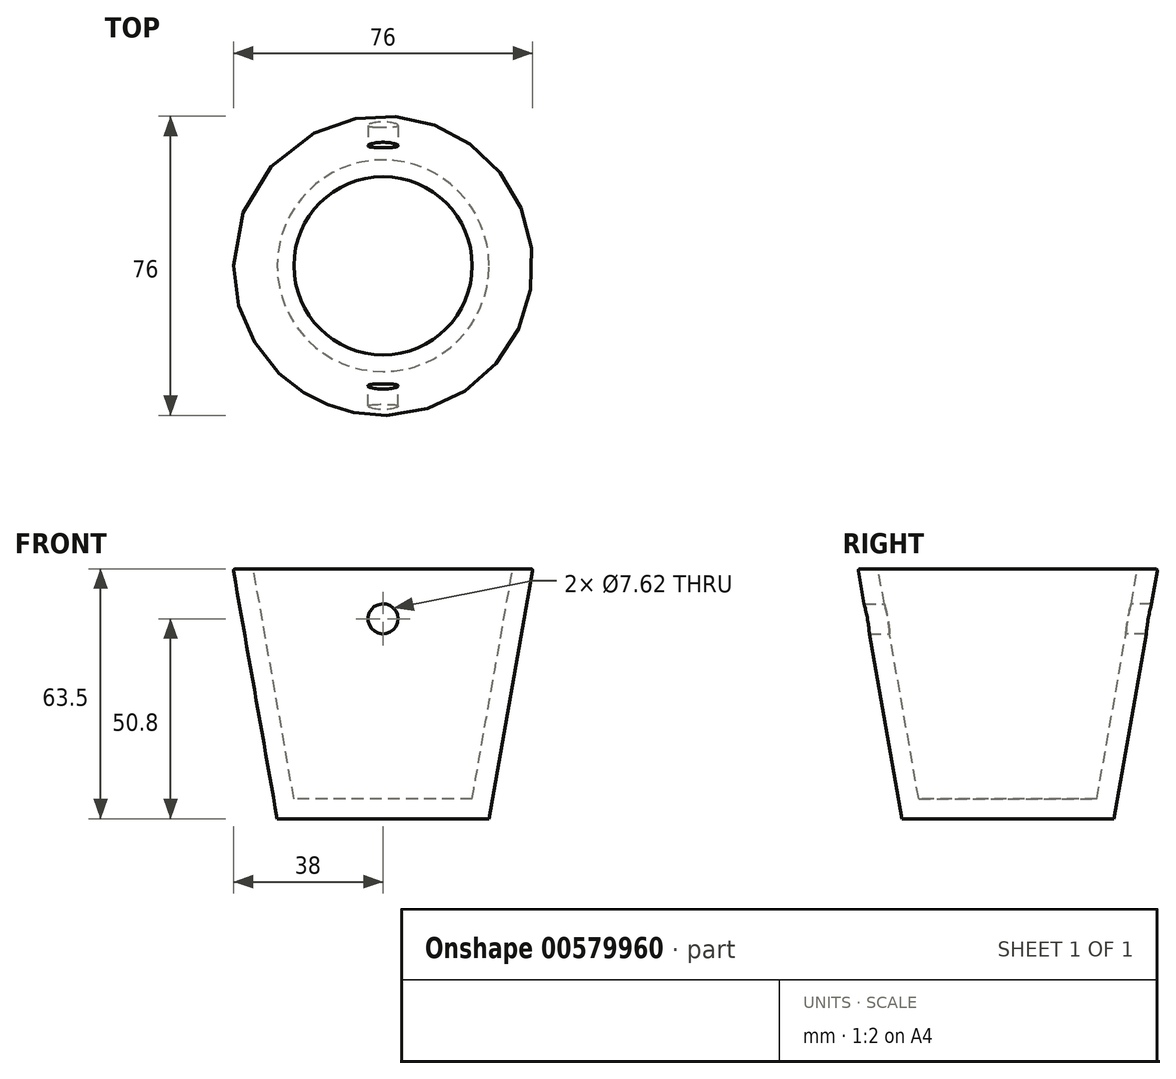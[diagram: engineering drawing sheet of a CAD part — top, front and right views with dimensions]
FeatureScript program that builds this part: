
annotation { "Feature Type Name" : "Feature", "Feature Type Description" : "" }
export const myFeature = defineFeature(function(context is Context, id is Id, definition is map)
    precondition{}
    {
        {
            var Q0;
            Q0=qCreatedBy(makeId("Front.planeOp"),FACE);
            var sketch = newSketch(context, id + "F0", { "sketchPlane" : qUnion([Q0])});
            skLineSegment(sketch, "E0", {"start": v(0, 63.5) * mm, "end": v(-38.1, 63.5) * mm});
            skLineSegment(sketch, "E1", {"start": v(-38.1, 63.5) * mm, "end": v(-26.9, 0) * mm});
            skLineSegment(sketch, "E2", {"start": v(-26.9, 0) * mm, "end": v(0, 0) * mm});
            skLineSegment(sketch, "E3", {"start": v(0, 0) * mm, "end": v(0, 63.5) * mm});
            skSolve(sketch);
        }
        {
            var Q0;
            Q0=makeQuery(id+"F0.imprint","IMPRINT",FACE,{"disambiguationData":[TD([[makeQuery(id+"F0.imprint","IMPRINT",EDGE,{"derivedFrom":sQuery(id+"F0.wireOp",EDGE,"E0")}),1.0]])]});
            var Q1;
            Q1=sQuery(id+"F0.wireOp",EDGE,"E3");
            revolve(context, id + "F1", {"entities" : qUnion([Q0]), "axis" : qUnion([Q1]), "revolveType" : RevolveType.FULL});
        }
        {
            var Q0;
            Q0=makeQuery(id+"F1.opRevolve","SWEPT_FACE",FACE,{"disambiguationData":[OSD([sQuery(id+"F0.wireOp",EDGE,"E0")])]});
            shell(context, id + "F2", {"entities" : qUnion([Q0]), "thickness" : 5.08 * mm});
        }
        {
            var Q0;
            Q0=qCreatedBy(makeId("Front.planeOp"),FACE);
            var sketch = newSketch(context, id + "F3", { "sketchPlane" : qUnion([Q0])});
            skLineSegment(sketch, "E4.0", {"start": v(38.1, 63.5) * mm, "end": v(-38.1, 63.5) * mm});
            skLineSegment(sketch, "E5", {"start": v(0, 63.5) * mm, "end": v(0, 50.8) * mm, "construction": true});
            skCircle(sketch, "E6", {"center": v(0, 50.8) * mm, "radius": 3.81 * mm});
            skSolve(sketch);
        }
        {
            var Q0;
            Q0=makeQuery(id+"F3.imprint","IMPRINT",FACE,{"disambiguationData":[TD([[makeQuery(id+"F3.imprint","IMPRINT",EDGE,{"derivedFrom":sQuery(id+"F3.wireOp",EDGE,"E6")}),1.0]])]});
            extrude(context, id + "F4", {"entities" : qUnion([Q0]), "operationType" : NewBodyOperationType.REMOVE, "oppositeDirection" : true, "depth" : 254 * mm, "offsetDistance" : 25.4 * mm});
        }
        {
            var Q0;
            Q0 = qSketchRegion(id + "F3", true);
            extrude(context, id + "F5", {"entities" : qUnion([Q0]), "operationType" : NewBodyOperationType.REMOVE, "depth" : 254 * mm, "offsetDistance" : 25.4 * mm});
        }
        {
            var Q0;
            Q0=makeQuery(id+"F1.opRevolve","SWEPT_EDGE",EDGE,{"disambiguationData":[OSD([sQuery(id+"F0.wireOp",EDGE,"E0"),sQuery(id+"F0.wireOp",EDGE,"E1")])]});
            var Q1;
            Q1=makeQuery(id+"F2.opShell","OFFSET_EDGE",EDGE,{"disambiguationData":[OSD([sQuery(id+"F0.wireOp",EDGE,"E0"),sQuery(id+"F0.wireOp",EDGE,"E1")])]});
            fillet(context, id + "F6", {"entities" : qUnion([Q0, Q1]), "radius" : 0.5 * mm, "tangentPropagation" : true, "allowEdgeOverflow" : false});
        }
    });
